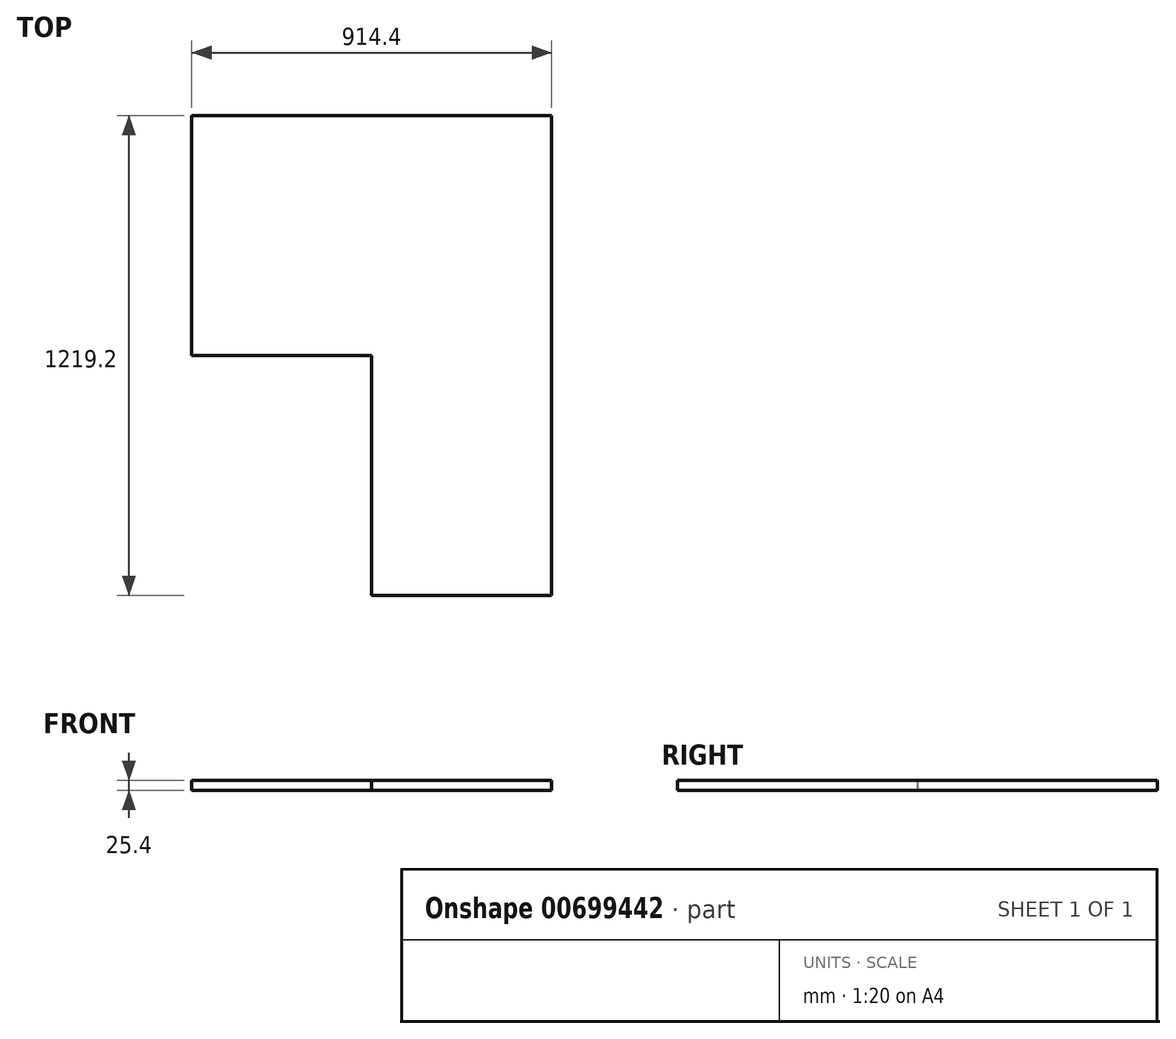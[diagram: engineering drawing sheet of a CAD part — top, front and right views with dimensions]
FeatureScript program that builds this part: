
annotation { "Feature Type Name" : "Feature", "Feature Type Description" : "" }
export const myFeature = defineFeature(function(context is Context, id is Id, definition is map)
    precondition{}
    {
        {
            var Q0;
            Q0=qCreatedBy(makeId("Top.planeOp"),FACE);
            var sketch = newSketch(context, id + "F0", { "sketchPlane" : qUnion([Q0])});
            skLineSegment(sketch, "E0", {"start": v(0, 0) * mm, "end": v(0, 609.6) * mm});
            skLineSegment(sketch, "E1", {"start": v(0, 609.6) * mm, "end": v(914.4, 609.6) * mm});
            skLineSegment(sketch, "E2", {"start": v(914.4, 609.6) * mm, "end": v(914.4, -609.6) * mm});
            skLineSegment(sketch, "E3", {"start": v(914.4, -609.6) * mm, "end": v(457.2, -609.6) * mm});
            skLineSegment(sketch, "E4", {"start": v(457.2, -609.6) * mm, "end": v(457.2, 0) * mm});
            skLineSegment(sketch, "E5", {"start": v(457.2, 0) * mm, "end": v(0, 0) * mm});
            skSolve(sketch);
        }
        {
            var Q0;
            Q0 = qSketchRegion(id + "F0", true);
            extrude(context, id + "F1", {"entities" : qUnion([Q0]), "depth" : 25.4 * mm, "offsetDistance" : 25.4 * mm});
        }
    });
